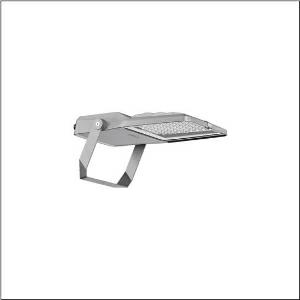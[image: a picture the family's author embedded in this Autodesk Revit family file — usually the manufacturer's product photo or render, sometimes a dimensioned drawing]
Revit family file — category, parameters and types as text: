
# Revit family: floodlight_fl_21_iq_mini___pl52_5xa7772c1d1a_38f0
name_source: partatom
category: Lighting Fixtures
units: mm (PartAtom-declared; Revit-internal decimal feet)

## family parameters
Cut with Voids When Loaded = No
Host = Face
Light Source = No
Part Type = Normal
Room Calculation Point = No
Round Connector Dimension = Use Diameter
Shared = No

## types (1)
- --- (1 x LED, 10110 lm, 87.2 W, 2200K)
    Apparent Load = 87 VA
    CIE Flux Codes = 26 60 98 100 100
    Color Rendering = 70
    Color Temperature = 2200K
    Default Elevation = 1800 mm
    Description = Floodlight FL 21 iQ mini, floodlight, primary light control with lens, of PMMA, primary optical cover: protective disc, of toughened safety glass, transparent, light distribution: PL52, light emission: direct distribution, installation type: surface-mounted, lamps: LED, High Power LED, rated values: 10.110lm | 87,2W | 115,9lm/W (begin service life); end service life: 10.110lm | 92,1W; at 50% lumin. flux: 5.055lm | 40,1W | 126,1lm/W, colour temperature: 2200K, colour rendering: CRI > 70, light colour: 722, light setting 1 begin service life: 100% | 10.110lm | 87,2W | 115,9lm/W | 2.200K, light setting 1 end service life: 92,1W, further light settings possible, control: Street-Remote, Auto-Match, Temp-Guard, Night-Set, Smart-Wire, Desk-Remote (wireless, voltage-free reading and setting of iQ features in the workshop via application-optimized NFC function/RFID function), optimised constant luminous flux control (CLO 2.0), pre-setting: linear dimming characteristic, with terminal, 6-pole, mains connection: 220..240V, AC, 50/60Hz, luminaire housing, of diecast aluminium, powder-coated, SITECO metallic grey (DB 702S), corrosivity category C5 mid according to DIN EN ISO 12944suitable for swimming poolschlorine-resistant, sealing non-destructively replaceable, mounting bracket, of steel, galvanised, powder-coated, SITECO metallic grey (DB 702S), protection rating (complete): IP66, insulation class (complete): insulation class II (safety insulation), certification: CE, ENEC, VDE, protection symbol: D, impact resistance: IK08, permissible operating ambient temperature: -40..+40°C, permissible operating ambient temperature for outdoor applications: -40..+50°C, standard: DIN EN 12944, LABS conformity tested according to VDMA 24364:2018-05, packaging unit: 1 piece

Light Distribution: PL52
    Height = 70 mm
    Lamp = 1 x LED
    Lamp Light Flux = 10110 lm
    Lamp Power = 87.2 W
    Lamp count = 1
    Length = 485 mm
    Luminous efficacy = 116 lm/W
    Manufacturer = Siteco
    ModVariant = No
    Model = 5XA7772C1D1A
    Number of Poles = 1
    OnlyDefault = Yes
    Power Factor = 1
    Product Name = Floodlight FL 21 iQ mini | PL52
    Product group = floodlight | pylon annexe
    ProductGroupID = 6201
    Protection Class = Protection class II
    Protection Degree = IP 66
    RLX_Detail_Level = 1
    RLX_Emergency_Light_Flux = 0 lm
    RLX_Emergency_Type = 0
    RLX_Emergency_Type_DB = No
    RlxData = <blob elided: 96781 chars, md5=3b3fc8d6>
    Socket = socket
    Standby Power = 0 W
    System Light Flux = 10110 lm
    System Power = 87 W
    Type Comments = factory setting: luminous flux: 100 % | dim-lin: 254 | 456 mA
    Type Image = l_1006845.jpg
    URL = http://relux.com
    VarID = @adj_163881
    Voltage = 0 V
    Weight = 0.00 kg
    Width = 337 mm

## geometry (parser evidence)
native form markers: Blend x4, Sweep x12
no freeform markers — native parametric forms only
